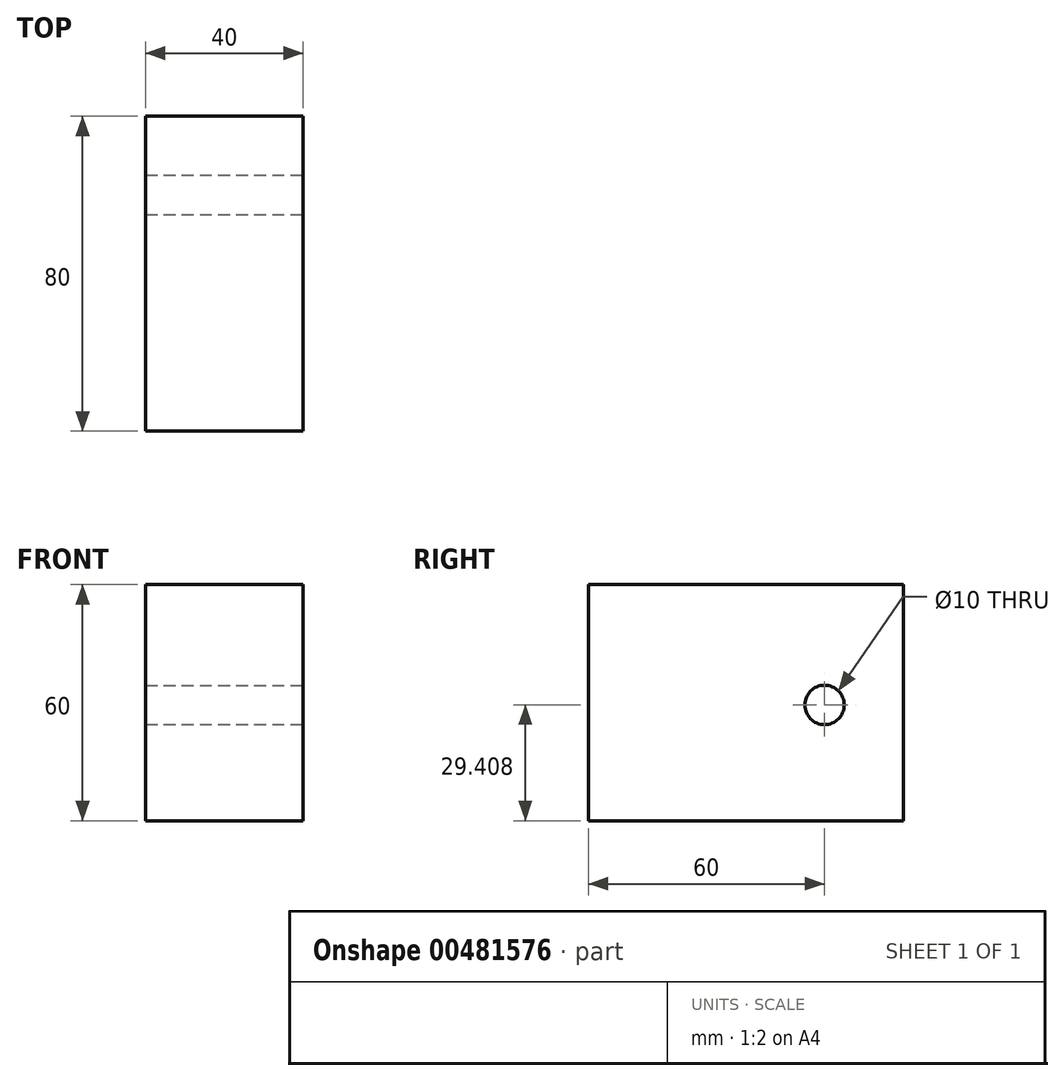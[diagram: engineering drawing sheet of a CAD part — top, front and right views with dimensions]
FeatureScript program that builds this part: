
annotation { "Feature Type Name" : "Feature", "Feature Type Description" : "" }
export const myFeature = defineFeature(function(context is Context, id is Id, definition is map)
    precondition{}
    {
        {
            var Q0;
            Q0=qCreatedBy(makeId("Top.planeOp"),FACE);
            var sketch = newSketch(context, id + "F0", { "sketchPlane" : qUnion([Q0])});
            skLineSegment(sketch, "E0.bottom", {"start": v(20, 40) * mm, "end": v(-20, 40) * mm});
            skLineSegment(sketch, "E0.top", {"start": v(20, -40) * mm, "end": v(-20, -40) * mm});
            skLineSegment(sketch, "E0.left", {"start": v(20, 40) * mm, "end": v(20, -40) * mm});
            skLineSegment(sketch, "E0.right", {"start": v(-20, 40) * mm, "end": v(-20, -40) * mm});
            skPoint(sketch, "E0.middle", {"position": v(0, 0) * mm});
            skSolve(sketch);
        }
        {
            var Q0;
            Q0 = qSketchRegion(id + "F0", true);
            extrude(context, id + "F1", {"entities" : qUnion([Q0]), "oppositeDirection" : true, "depth" : 60 * mm});
        }
        {
            var Q0;
            Q0=makeQuery(id+"F1.opExtrude","SWEPT_FACE",FACE,{"disambiguationData":[OSD([sQuery(id+"F0.wireOp",EDGE,"E0.left")])]});
            var sketch = newSketch(context, id + "F2", { "sketchPlane" : qUnion([Q0])});
            skCircle(sketch, "E1", {"center": v(20, -30.6) * mm, "radius": 5 * mm});
            skSolve(sketch);
        }
        {
            var Q0;
            Q0=makeQuery(id+"F2.imprint","IMPRINT",FACE,{"disambiguationData":[TD([[makeQuery(id+"F2.imprint","IMPRINT",EDGE,{"derivedFrom":sQuery(id+"F2.wireOp",EDGE,"E1")}),1.0]])]});
            extrude(context, id + "F3", {"entities" : qUnion([Q0]), "operationType" : NewBodyOperationType.REMOVE, "endBound" : BoundingType.THROUGH_ALL, "oppositeDirection" : true, "depth" : 25 * mm});
        }
    });
